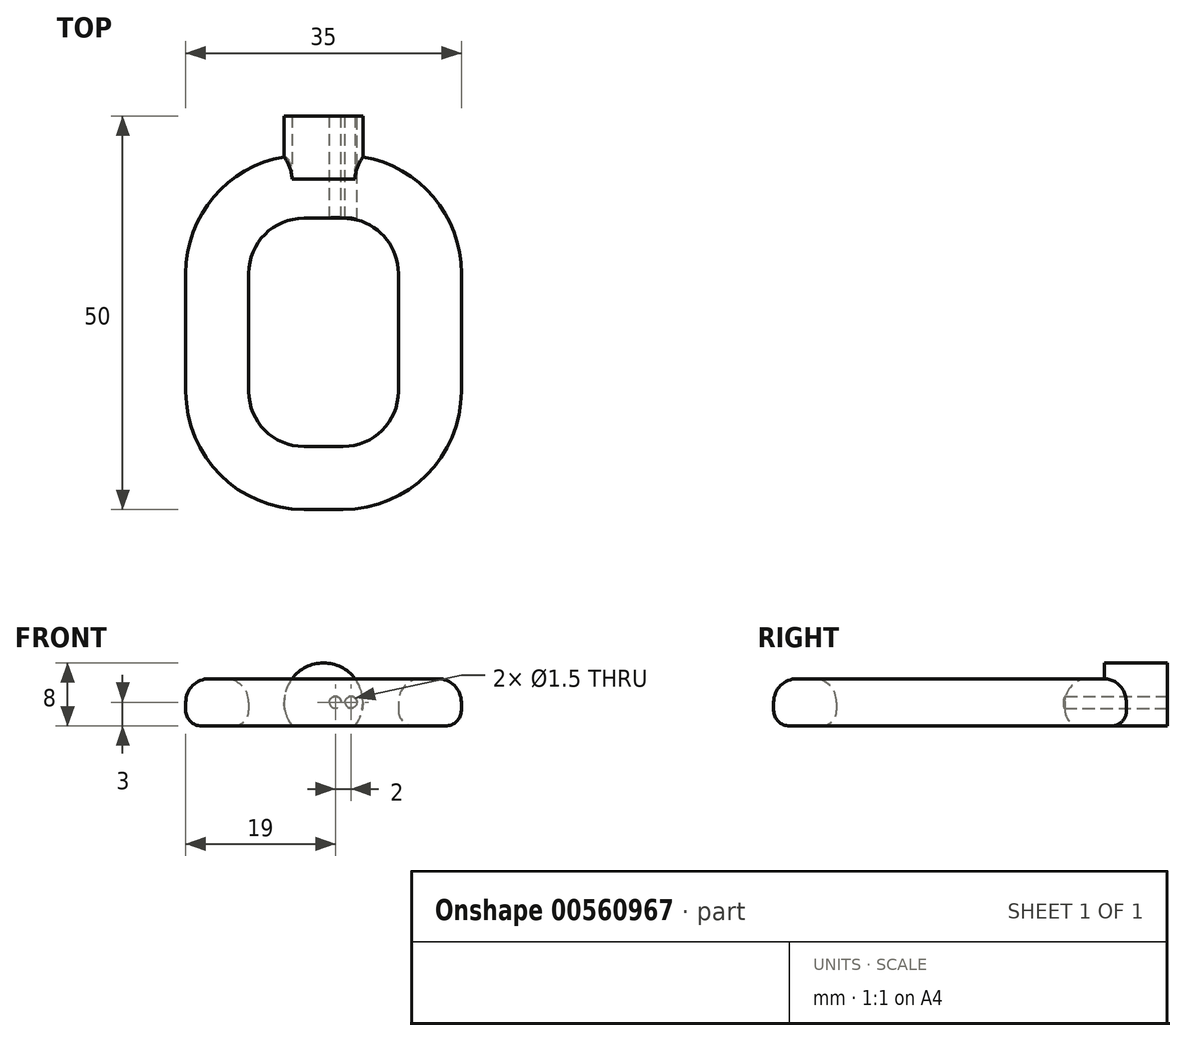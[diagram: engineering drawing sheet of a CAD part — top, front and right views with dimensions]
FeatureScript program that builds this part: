
annotation { "Feature Type Name" : "Feature", "Feature Type Description" : "" }
export const myFeature = defineFeature(function(context is Context, id is Id, definition is map)
    precondition{}
    {
        {
            var Q0;
            Q0=qCreatedBy(makeId("Top.planeOp"),FACE);
            var sketch = newSketch(context, id + "F0", { "sketchPlane" : qUnion([Q0])});
            skLineSegment(sketch, "E0.bottom", {"start": v(2.5, 22.5) * mm, "end": v(-2.5, 22.5) * mm});
            skLineSegment(sketch, "E0.top", {"start": v(2.5, -22.5) * mm, "end": v(-2.5, -22.5) * mm});
            skLineSegment(sketch, "E0.left", {"start": v(17.5, 7.5) * mm, "end": v(17.5, -7.5) * mm});
            skLineSegment(sketch, "E0.right", {"start": v(-17.5, 7.5) * mm, "end": v(-17.5, -7.5) * mm});
            skPoint(sketch, "E0.middle", {"position": v(0, 0) * mm});
            skPoint(sketch, "E1.visualSharp", {"position": v(-17.5, 22.5) * mm});
            skArc(sketch, "E1.filletArc", {"start": v(-2.5, 22.5) * mm, "mid": v(-13.1, 18.1) * mm, "end": v(-17.5, 7.5) * mm});
            skPoint(sketch, "E2.visualSharp", {"position": v(17.5, 22.5) * mm});
            skArc(sketch, "E2.filletArc", {"start": v(17.5, 7.5) * mm, "mid": v(13.1, 18.1) * mm, "end": v(2.5, 22.5) * mm});
            skPoint(sketch, "E3.visualSharp", {"position": v(17.5, -22.5) * mm});
            skArc(sketch, "E3.filletArc", {"start": v(2.5, -22.5) * mm, "mid": v(13.1, -18.1) * mm, "end": v(17.5, -7.5) * mm});
            skPoint(sketch, "E4.visualSharp", {"position": v(-17.5, -22.5) * mm});
            skArc(sketch, "E4.filletArc", {"start": v(-17.5, -7.5) * mm, "mid": v(-13.1, -18.1) * mm, "end": v(-2.5, -22.5) * mm});
            skArc(sketch, "E5.0", {"start": v(9.5, 7.5) * mm, "mid": v(7.45, 12.45) * mm, "end": v(2.5, 14.5) * mm});
            skLineSegment(sketch, "E5.1", {"start": v(9.5, 7.5) * mm, "end": v(9.5, -7.5) * mm});
            skLineSegment(sketch, "E5.2", {"start": v(2.5, 14.5) * mm, "end": v(-2.5, 14.5) * mm});
            skArc(sketch, "E5.3", {"start": v(2.5, -14.5) * mm, "mid": v(7.45, -12.45) * mm, "end": v(9.5, -7.5) * mm});
            skArc(sketch, "E5.4", {"start": v(-2.5, 14.5) * mm, "mid": v(-7.45, 12.45) * mm, "end": v(-9.5, 7.5) * mm});
            skLineSegment(sketch, "E5.5", {"start": v(-9.5, 7.5) * mm, "end": v(-9.5, -7.5) * mm});
            skArc(sketch, "E5.6", {"start": v(-9.5, -7.5) * mm, "mid": v(-7.45, -12.45) * mm, "end": v(-2.5, -14.5) * mm});
            skLineSegment(sketch, "E5.7", {"start": v(2.5, -14.5) * mm, "end": v(-2.5, -14.5) * mm});
            skSolve(sketch);
        }
        {
            var Q0;
            Q0=makeQuery(id+"F0.imprint","IMPRINT",FACE,{"disambiguationData":[TD([[makeQuery(id+"F0.imprint","IMPRINT",EDGE,{"derivedFrom":sQuery(id+"F0.wireOp",EDGE,"E0.bottom")}),1.0]])]});
            extrude(context, id + "F1", {"entities" : qUnion([Q0]), "depth" : 6 * mm, "offsetDistance" : 25 * mm, "symmetric" : true});
        }
        {
            var Q0;
            Q0=makeQuery(id+"F1.opExtrude","CAP_EDGE",EDGE,{"disambiguationData":[OSD([sQuery(id+"F0.wireOp",EDGE,"E0.right")])],"isStart":true});
            var Q1;
            Q1=makeQuery(id+"F1.opExtrude","CAP_EDGE",EDGE,{"disambiguationData":[OSD([sQuery(id+"F0.wireOp",EDGE,"E5.3")])],"isStart":true});
            var Q2;
            Q2=makeQuery(id+"F1.opExtrude","CAP_EDGE",EDGE,{"disambiguationData":[OSD([sQuery(id+"F0.wireOp",EDGE,"E5.1")])],"isStart":true});
            fillet(context, id + "F2", {"entities" : qUnion([Q0, Q1, Q2]), "radius" : 2 * mm, "tangentPropagation" : true, "allowEdgeOverflow" : false});
        }
        {
            var Q0;
            Q0=makeQuery(id+"F1.opExtrude","CAP_EDGE",EDGE,{"disambiguationData":[OSD([sQuery(id+"F0.wireOp",EDGE,"E0.bottom")])],"isStart":false});
            var Q1;
            Q1=makeQuery(id+"F1.opExtrude","CAP_EDGE",EDGE,{"disambiguationData":[OSD([sQuery(id+"F0.wireOp",EDGE,"E5.0")])],"isStart":false});
            fillet(context, id + "F3", {"entities" : qUnion([Q0, Q1]), "radius" : 3 * mm, "tangentPropagation" : true, "allowEdgeOverflow" : false});
        }
        {
            var Q0;
            Q0=makeQuery(id+"F1.opExtrude","SWEPT_FACE",FACE,{"disambiguationData":[OSD([sQuery(id+"F0.wireOp",EDGE,"E0.bottom")])]});
            var sketch = newSketch(context, id + "F4", { "sketchPlane" : qUnion([Q0])});
            skCircle(sketch, "E6", {"center": v(0, 0) * mm, "radius": 5 * mm});
            skSolve(sketch);
        }
        {
            var Q0;
            Q0=makeQuery(id+"F4.imprint","IMPRINT",FACE,{"disambiguationData":[TD([[makeQuery(id+"F4.imprint","IMPRINT",EDGE,{"derivedFrom":sQuery(id+"F4.wireOp",EDGE,"E6")}),1.0]])]});
            var Q1;
            {var subQ0=sQuery(id+"F0.wireOp",EDGE,"E0.bottom");var subQ1=makeQuery(id+"F1.opExtrude","SWEPT_FACE",FACE,{"disambiguationData":[OSD([subQ0])]});Q1=makeQuery(id+"F4.imprint","IMPRINT",FACE,{"disambiguationData":[TD([[makeQuery(id+"F4.imprint","IMPRINT",EDGE,{"derivedFrom":makeQuery(id+"F2.opFillet","BLEND_EDGE",EDGE,{"blendedFrom":[makeQuery(id+"F1.opExtrude","CAP_EDGE",EDGE,{"disambiguationData":[OSD([subQ0])],"isStart":true}),subQ1],"blendedInto":[subQ1]})}),1.0]])]});}
            extrude(context, id + "F5", {"entities" : qUnion([Q0, Q1]), "operationType" : NewBodyOperationType.ADD, "depth" : 5 * mm, "offsetDistance" : 25 * mm, "hasSecondDirection" : true, "secondDirectionOppositeDirection" : true, "secondDirectionDepth" : 3 * mm});
        }
        {
            var Q0;
            Q0=makeQuery(id+"F5.opExtrude","CAP_FACE",FACE,{"disambiguationData":[OSD([sQuery(id+"F4.wireOp",EDGE,"E6")])],"isStart":false});
            var sketch = newSketch(context, id + "F6", { "sketchPlane" : qUnion([Q0])});
            skPoint(sketch, "E7", {"position": v(-1.5, 0) * mm});
            skPoint(sketch, "E8", {"position": v(-3.5, 0) * mm});
            skSolve(sketch);
        }
        {
            var Q0;
            Q0=sQuery(id+"F6.wireOp",VERTEX,"E8");
            var Q1;
            Q1=sQuery(id+"F6.wireOp",VERTEX,"E7");
            var Q2;
            Q2=makeQuery(id+"F1.opExtrude","SWEPT_BODY",BODY,{"disambiguationData":[OSD([sQuery(id+"F0.wireOp",EDGE,"E0.bottom"),sQuery(id+"F0.wireOp",EDGE,"E0.top"),sQuery(id+"F0.wireOp",EDGE,"E0.left"),sQuery(id+"F0.wireOp",EDGE,"E0.right"),sQuery(id+"F0.wireOp",EDGE,"E1.filletArc"),sQuery(id+"F0.wireOp",EDGE,"E2.filletArc"),sQuery(id+"F0.wireOp",EDGE,"E3.filletArc"),sQuery(id+"F0.wireOp",EDGE,"E4.filletArc"),sQuery(id+"F0.wireOp",EDGE,"E5.0"),sQuery(id+"F0.wireOp",EDGE,"E5.1"),sQuery(id+"F0.wireOp",EDGE,"E5.2"),sQuery(id+"F0.wireOp",EDGE,"E5.3"),sQuery(id+"F0.wireOp",EDGE,"E5.4"),sQuery(id+"F0.wireOp",EDGE,"E5.5"),sQuery(id+"F0.wireOp",EDGE,"E5.6"),sQuery(id+"F0.wireOp",EDGE,"E5.7")])]});
            hole(context, id + "F7", {"style" : HoleStyle.SIMPLE, "endStyle" : HoleEndStyle.BLIND, "holeDiameter" : 1.5 * mm, "majorDiameter" : 5 * mm, "holeDepth" : 20 * mm, "isTappedThrough" : true, "tappedDepth" : 12 * mm, "tapClearance" : 3, "locations" : qUnion([Q0, Q1]), "scope" : qUnion([Q2])});
        }
        {
            var Q0;
            Q0=makeQuery(id+"F5.boolean.opBoolean","INTERSECT",EDGE,{"derivedFrom":[makeQuery(id+"F1.opExtrude","CAP_FACE",FACE,{"disambiguationData":[OSD([sQuery(id+"F0.wireOp",EDGE,"E0.bottom"),sQuery(id+"F0.wireOp",EDGE,"E0.top"),sQuery(id+"F0.wireOp",EDGE,"E0.left"),sQuery(id+"F0.wireOp",EDGE,"E0.right"),sQuery(id+"F0.wireOp",EDGE,"E1.filletArc"),sQuery(id+"F0.wireOp",EDGE,"E2.filletArc"),sQuery(id+"F0.wireOp",EDGE,"E3.filletArc"),sQuery(id+"F0.wireOp",EDGE,"E4.filletArc"),sQuery(id+"F0.wireOp",EDGE,"E5.0"),sQuery(id+"F0.wireOp",EDGE,"E5.1"),sQuery(id+"F0.wireOp",EDGE,"E5.2"),sQuery(id+"F0.wireOp",EDGE,"E5.3"),sQuery(id+"F0.wireOp",EDGE,"E5.4"),sQuery(id+"F0.wireOp",EDGE,"E5.5"),sQuery(id+"F0.wireOp",EDGE,"E5.6"),sQuery(id+"F0.wireOp",EDGE,"E5.7")])],"isStart":true}),makeQuery(id+"F5.opExtrude","CAP_FACE",FACE,{"disambiguationData":[OSD([sQuery(id+"F4.wireOp",EDGE,"E6")])],"isStart":true})]});
            var Q1;
            {var subQ0=sQuery(id+"F0.wireOp",EDGE,"E0.bottom");Q1=makeQuery(id+"F3.opFillet","BLEND_EDGE",EDGE,{"blendedFrom":[makeQuery(id+"F1.opExtrude","CAP_EDGE",EDGE,{"disambiguationData":[OSD([subQ0])],"isStart":false}),makeQuery(id+"F1.opExtrude","CAP_FACE",FACE,{"disambiguationData":[OSD([subQ0,sQuery(id+"F0.wireOp",EDGE,"E0.top"),sQuery(id+"F0.wireOp",EDGE,"E0.left"),sQuery(id+"F0.wireOp",EDGE,"E0.right"),sQuery(id+"F0.wireOp",EDGE,"E1.filletArc"),sQuery(id+"F0.wireOp",EDGE,"E2.filletArc"),sQuery(id+"F0.wireOp",EDGE,"E3.filletArc"),sQuery(id+"F0.wireOp",EDGE,"E4.filletArc"),sQuery(id+"F0.wireOp",EDGE,"E5.0"),sQuery(id+"F0.wireOp",EDGE,"E5.1"),sQuery(id+"F0.wireOp",EDGE,"E5.2"),sQuery(id+"F0.wireOp",EDGE,"E5.3"),sQuery(id+"F0.wireOp",EDGE,"E5.4"),sQuery(id+"F0.wireOp",EDGE,"E5.5"),sQuery(id+"F0.wireOp",EDGE,"E5.6"),sQuery(id+"F0.wireOp",EDGE,"E5.7")])],"isStart":false})],"blendedInto":[makeQuery(id+"F1.opExtrude","CAP_FACE",FACE,{"disambiguationData":[OSD([subQ0,sQuery(id+"F0.wireOp",EDGE,"E0.top"),sQuery(id+"F0.wireOp",EDGE,"E0.left"),sQuery(id+"F0.wireOp",EDGE,"E0.right"),sQuery(id+"F0.wireOp",EDGE,"E1.filletArc"),sQuery(id+"F0.wireOp",EDGE,"E2.filletArc"),sQuery(id+"F0.wireOp",EDGE,"E3.filletArc"),sQuery(id+"F0.wireOp",EDGE,"E4.filletArc"),sQuery(id+"F0.wireOp",EDGE,"E5.0"),sQuery(id+"F0.wireOp",EDGE,"E5.1"),sQuery(id+"F0.wireOp",EDGE,"E5.2"),sQuery(id+"F0.wireOp",EDGE,"E5.3"),sQuery(id+"F0.wireOp",EDGE,"E5.4"),sQuery(id+"F0.wireOp",EDGE,"E5.5"),sQuery(id+"F0.wireOp",EDGE,"E5.6"),sQuery(id+"F0.wireOp",EDGE,"E5.7")])],"isStart":false})]});}
            fillet(context, id + "F8", {"entities" : qUnion([Q0, Q1]), "radius" : 1.5 * mm, "tangentPropagation" : true, "allowEdgeOverflow" : false});
        }
        {
            var Q0;
            Q0=makeQuery(id+"F1.opExtrude","CAP_FACE",FACE,{"disambiguationData":[OSD([sQuery(id+"F0.wireOp",EDGE,"E0.bottom"),sQuery(id+"F0.wireOp",EDGE,"E0.top"),sQuery(id+"F0.wireOp",EDGE,"E0.left"),sQuery(id+"F0.wireOp",EDGE,"E0.right"),sQuery(id+"F0.wireOp",EDGE,"E1.filletArc"),sQuery(id+"F0.wireOp",EDGE,"E2.filletArc"),sQuery(id+"F0.wireOp",EDGE,"E3.filletArc"),sQuery(id+"F0.wireOp",EDGE,"E4.filletArc"),sQuery(id+"F0.wireOp",EDGE,"E5.0"),sQuery(id+"F0.wireOp",EDGE,"E5.1"),sQuery(id+"F0.wireOp",EDGE,"E5.2"),sQuery(id+"F0.wireOp",EDGE,"E5.3"),sQuery(id+"F0.wireOp",EDGE,"E5.4"),sQuery(id+"F0.wireOp",EDGE,"E5.5"),sQuery(id+"F0.wireOp",EDGE,"E5.6"),sQuery(id+"F0.wireOp",EDGE,"E5.7")])],"isStart":true});
            var sketch = newSketch(context, id + "F9", { "sketchPlane" : qUnion([Q0])});
            skLineSegment(sketch, "E9.bottom", {"start": v(-5, -16.96) * mm, "end": v(6.36, -16.96) * mm});
            skLineSegment(sketch, "E9.top", {"start": v(-5, -29.58) * mm, "end": v(6.36, -29.58) * mm});
            skLineSegment(sketch, "E9.left", {"start": v(-5, -16.96) * mm, "end": v(-5, -29.58) * mm});
            skLineSegment(sketch, "E9.right", {"start": v(6.36, -16.96) * mm, "end": v(6.36, -29.58) * mm});
            skSolve(sketch);
        }
        {
            var Q0;
            {var subQ6=sQuery(id+"F9.wireOp",EDGE,"E9.top");Q0=makeQuery(id+"F9.imprint","IMPRINT",FACE,{"disambiguationData":[TD([[makeQuery(id+"F9.imprint","IMPRINT",EDGE,{"derivedFrom":subQ6}),1.0]])]});}
            extrude(context, id + "F10", {"entities" : qUnion([Q0]), "operationType" : NewBodyOperationType.REMOVE, "depth" : 25 * mm, "offsetDistance" : 25 * mm});
        }
    });
